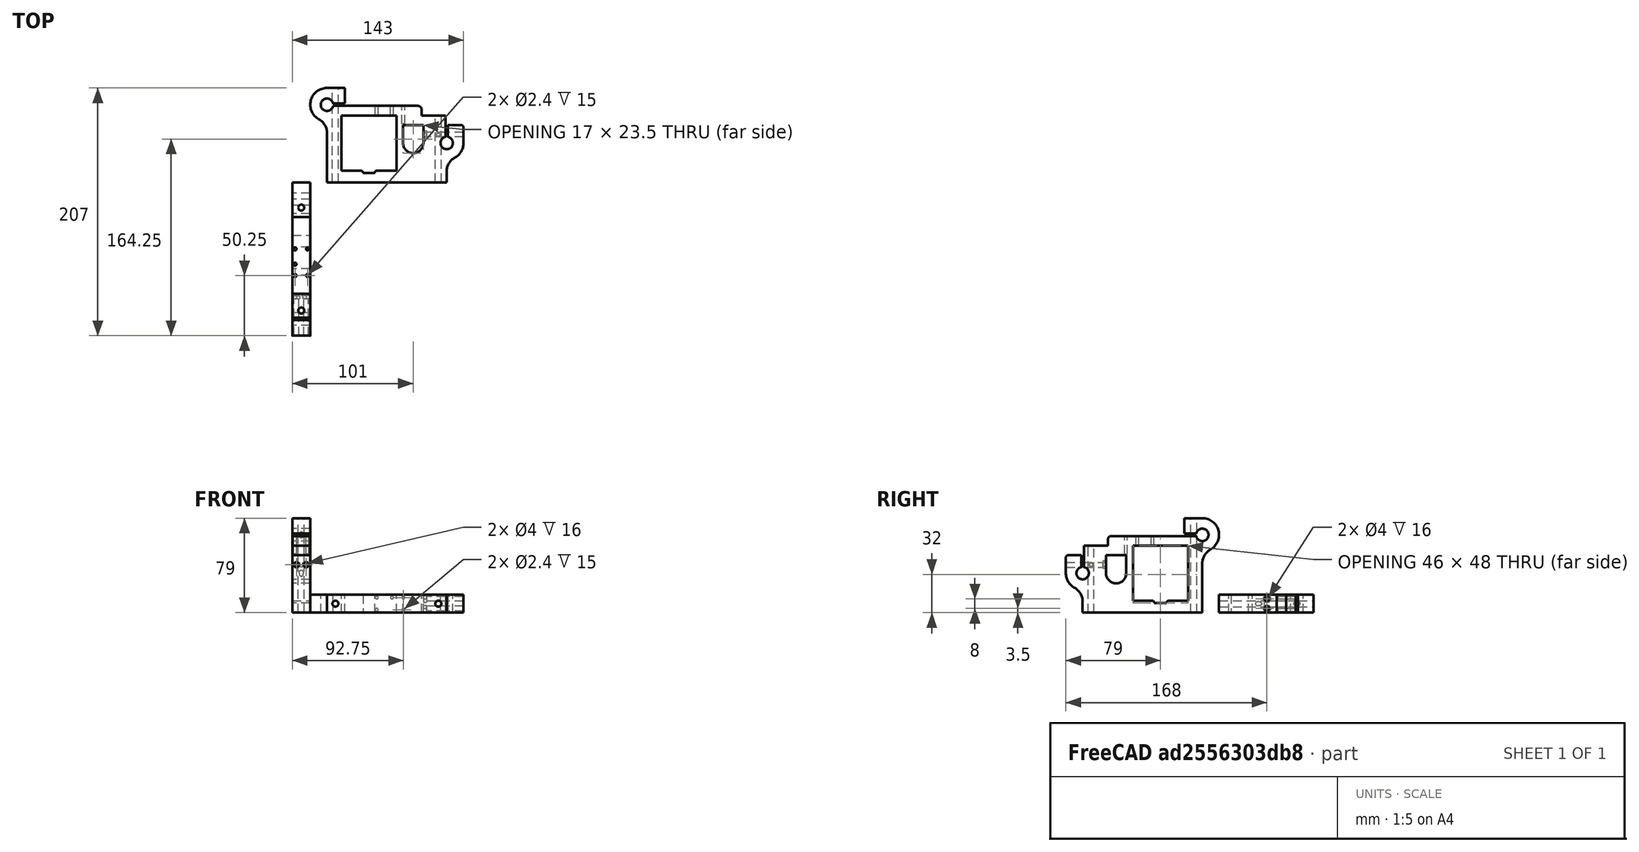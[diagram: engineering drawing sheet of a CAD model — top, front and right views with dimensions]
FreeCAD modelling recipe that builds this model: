
FCSTD DOCUMENT  (FreeCAD 0.15R4630 (Git))
Label: x_left_holder
License: All rights reserved
LicenseURL: http://en.wikipedia.org/wiki/All_rights_reserved
objects: Part::Cylinder×14, Part::Box×9, Part::Cut×9, Part::MultiFuse×8, Part::Fillet×4, Part::Feature×2, Part::Prism×2, Mesh::Feature×1
note: 48 computed .brp shape members not serialized (recipe doc carries the construction recipe); baked Part::Feature solids carry a one-line shape summary decoded from their .brp

FEATURE [Mesh::Feature] XholderLeft
FEATURE [Part::Feature] XholderLeft001001  label="XholderLeft002"
  shape: bbox 128 x 79.02 x 15 mm, 1651 faces, 0 solids (baked)
FEATURE [Part::Box] Box  label="Cubo"
  Height = 15
  Length = 100
  Placement = pos=(14,0,0) rot=(0,0,1;0rad)
  Width = 56
FEATURE [Part::Box] Box001  label="Cubo001"
  Height = 15
  Length = 15
  Placement = pos=(14,56,0) rot=(0,0,1;0rad)
  Width = 23
FEATURE [Part::Box] Box002  label="Cubo002"
  Height = 15
  Length = 64
  Placement = pos=(29,56,0) rot=(0,0,1;0rad)
  Width = 8
FEATURE [Part::Box] Box003  label="Cubo003"
  Height = 15
  Length = 14
  Placement = pos=(114,33,0) rot=(0,0,1;0rad)
  Width = 15
FEATURE [Part::Cylinder] Cylinder  label="Cilindro"
  Angle = 360
  Height = 15
  Placement = pos=(14,65,0) rot=(0,0,1;0rad)
  Radius = 14
FEATURE [Part::Cylinder] Cylinder001  label="Cilindro001"
  Angle = 360
  Height = 15
  Placement = pos=(114,33,0) rot=(0,0,1;0rad)
  Radius = 14
FEATURE [Part::MultiFuse] Fusion
  Shapes = -> [Box,Cylinder001,Cylinder,Box003,Box002,Box001]
FEATURE [Part::Box] Box004  label="Cubo004"
  Height = 15
  Length = 46
  Placement = pos=(26,10,0) rot=(0,0,1;0rad)
  Width = 46
FEATURE [Part::Cut] Cut
  Base = -> Fusion
  Tool = -> Box004
FEATURE [Part::Fillet] Fillet
  Base = -> Cut
  Edges = 2 edges r=13: [Edge60,Edge63]
FEATURE [Part::Fillet] Fillet001
  Base = -> Fillet
  Edges = 1 edges r=3: [Edge76]
FEATURE [Part::Fillet] Fillet002
  Base = -> Fillet001
  Edges = 1 edges r=2: [Edge89]
FEATURE [Part::Cylinder] Cylinder002  label="Cilindro002"
  Angle = 360
  Height = 17
  Placement = pos=(14,65,-1) rot=(0,0,1;0rad)
  Radius = 5.2
FEATURE [Part::Cylinder] Cylinder003  label="Cilindro003"
  Angle = 360
  Height = 17
  Placement = pos=(114,33,-1) rot=(0,0,1;0rad)
  Radius = 5.2
FEATURE [Part::MultiFuse] Fusion001
  Shapes = -> [Cylinder002,Cylinder003]
FEATURE [Part::Cut] Cut001
  Base = -> Fillet002
  Tool = -> Fusion001
FEATURE [Part::Box] Box005  label="Cubo005"
  Height = 15
  Length = 10
  Placement = pos=(44,8,0) rot=(0,0,1;0rad)
  Width = 3
FEATURE [Part::Cut] Cut002
  Base = -> Cut001
  Tool = -> Box005
FEATURE [Part::Fillet] Fillet003
  Base = -> Cut002
  Edges = 2 edges r=1.9: [Edge61,Edge68]
FEATURE [Part::Box] Box006  label="Cubo006"
  Height = 15
  Length = 17
  Placement = pos=(77.5,33,0) rot=(0,0,1;0rad)
  Width = 15
FEATURE [Part::Cylinder] Cylinder004  label="Cilindro004"
  Angle = 360
  Height = 15
  Placement = pos=(86,33,0) rot=(0,0,1;0rad)
  Radius = 8.5
FEATURE [Part::MultiFuse] Fusion002
  Shapes = -> [Box006,Cylinder004]
FEATURE [Part::Cut] Cut003
  Base = -> Fillet003
  Tool = -> Fusion002
FEATURE [Part::Box] Box007  label="Cubo007"
  Height = 17
  Length = 12
  Placement = pos=(18,64,-1) rot=(0,0,1;0rad)
  Width = 2
FEATURE [Part::Box] Box008  label="Cubo008"
  Height = 17
  Length = 2
  Placement = pos=(113,37,-1) rot=(0,0,1;0rad)
  Width = 20
FEATURE [Part::MultiFuse] Fusion003
  Shapes = -> [Box007,Box008]
FEATURE [Part::Cut] Cut004
  Base = -> Cut003
  Tool = -> Fusion003
FEATURE [Part::Cylinder] Cylinder005  label="Cilindro005"
  Angle = 360
  Height = 81
  Placement = pos=(21,-1,7.5) rot=(-1,0,0;1.5708rad)
  Radius = 2.5
FEATURE [Part::Cylinder] Cylinder006  label="Cilindro006"
  Angle = 360
  Height = 58
  Placement = pos=(107,-1,7.5) rot=(-1,0,0;1.5708rad)
  Radius = 2.5
FEATURE [Part::MultiFuse] Fusion004
  Shapes = -> [Cylinder005,Cylinder006]
FEATURE [Part::Cut] Cut005
  Base = -> Cut004
  Tool = -> Fusion004
FEATURE [Part::Cylinder] Cylinder007  label="Cilindro007"
  Angle = 360
  Height = 35
  Placement = pos=(129,40,3.5) rot=(0,-1,0;1.5708rad)
  Radius = 2
FEATURE [Part::Cylinder] Cylinder008  label="Cilindro008"
  Angle = 360
  Height = 35
  Placement = pos=(129,40,11.5) rot=(0,-1,0;1.5708rad)
  Radius = 2
FEATURE [Part::MultiFuse] Fusion005
  Shapes = -> [Cylinder007,Cylinder008]
FEATURE [Part::Cut] Cut006
  Base = -> Cut005
  Tool = -> Fusion005
FEATURE [Part::Prism] Prism  label="Prisma"
  Circumradius = 3.2
  Height = 3
  Placement = pos=(94,40,3.5) rot=(0.250563,0.935113,0.250563;1.63783rad)
  Polygon = 6
FEATURE [Part::Prism] Prism001  label="Prisma001"
  Circumradius = 3.2
  Height = 3
  Placement = pos=(94,40,11.5) rot=(0.250563,0.935113,0.250563;1.63783rad)
  Polygon = 6
FEATURE [Part::MultiFuse] Fusion006
  Shapes = -> [Prism,Prism001]
FEATURE [Part::Cut] Cut007
  Base = -> Cut006
  Tool = -> Fusion006
FEATURE [Part::Cylinder] Cylinder009  label="Cilindro009"
  Angle = 360
  Height = 10
  Placement = pos=(55.55,55,2.35) rot=(-1,0,0;1.5708rad)
  Radius = 1.2
FEATURE [Part::Cylinder] Cylinder010  label="Cilindro010"
  Angle = 360
  Height = 10
  Placement = pos=(68.25,55,12.65) rot=(-1,0,0;1.5708rad)
  Radius = 1.2
FEATURE [Part::Cylinder] Cylinder011  label="Cilindro011"
  Angle = 360
  Height = 10
  Placement = pos=(55.55,55,12.65) rot=(-1,0,0;1.5708rad)
  Radius = 1.2
FEATURE [Part::Cylinder] Cylinder012  label="Cilindro012"
  Angle = 360
  Height = 16
  Placement = pos=(77.75,49,12.65) rot=(-1,0,0;1.5708rad)
  Radius = 1.2
FEATURE [Part::Cylinder] Cylinder013  label="Cilindro013"
  Angle = 360
  Height = 16
  Placement = pos=(77.75,49,2.35) rot=(-1,0,0;1.5708rad)
  Radius = 1.2
FEATURE [Part::MultiFuse] Fusion007
  Shapes = -> [Cylinder009,Cylinder013,Cylinder010,Cylinder011,Cylinder012]
FEATURE [Part::Cut] Cut008  label="x_left_holder"
  Base = -> Cut007
  Tool = -> Fusion007
FEATURE [Part::Feature] Cut009  label="x_left_holder001"
  Placement = pos=(0,0,0) rot=(0.57735,-0.57735,-0.57735;2.0944rad)
  shape: bbox 15 x 128 x 79 mm, 65 faces (baked)
